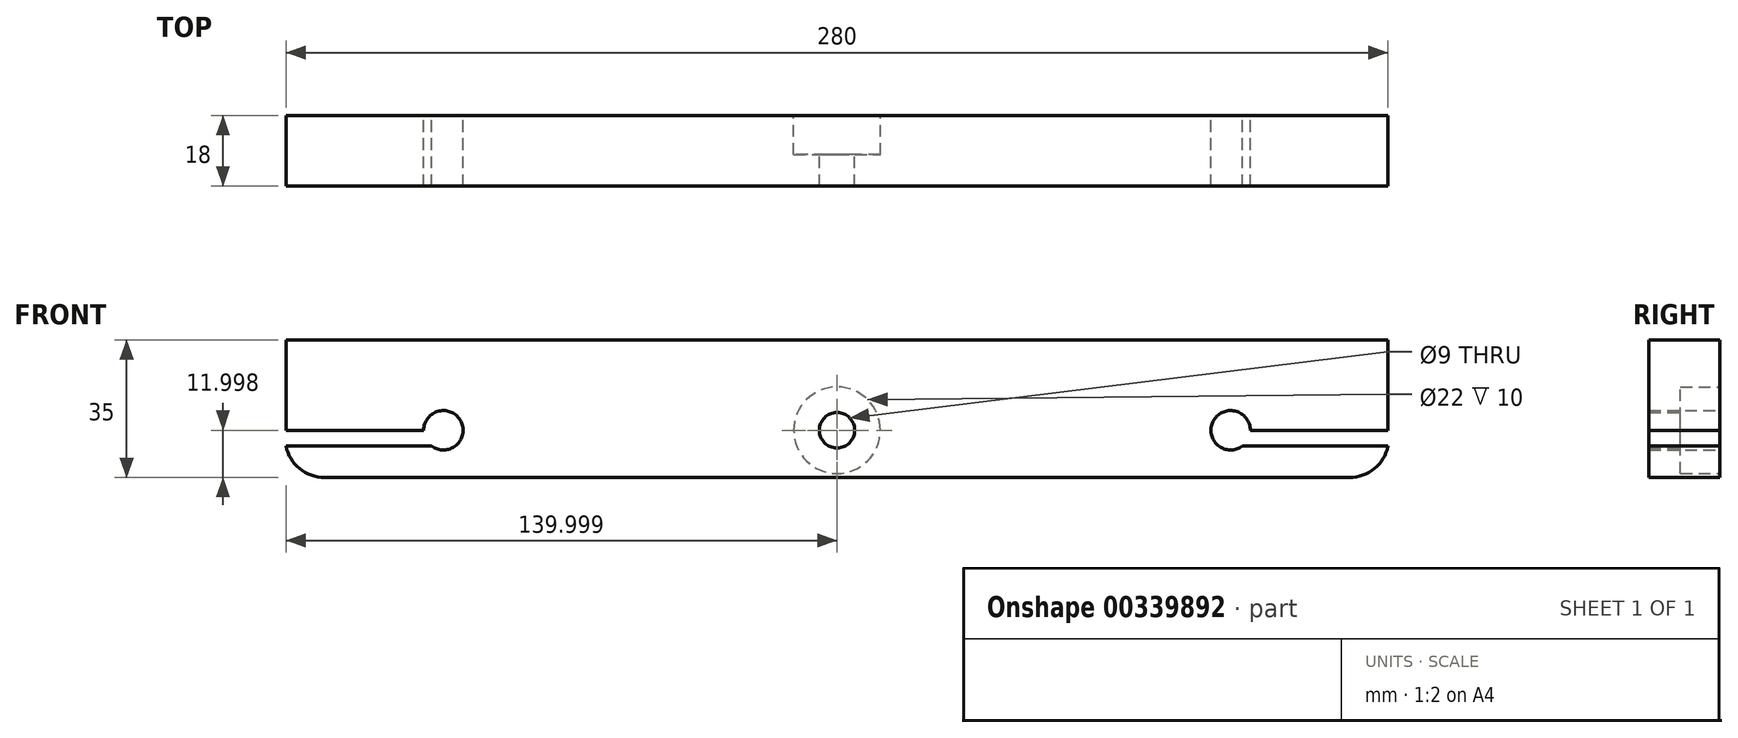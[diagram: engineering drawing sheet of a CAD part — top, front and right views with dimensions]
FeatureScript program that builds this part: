
annotation { "Feature Type Name" : "Feature", "Feature Type Description" : "" }
export const myFeature = defineFeature(function(context is Context, id is Id, definition is map)
    precondition{}
    {
        {
            var Q0;
            Q0=qCreatedBy(makeId("Front.planeOp"),FACE);
            var sketch = newSketch(context, id + "F0", { "sketchPlane" : qUnion([Q0])});
            skLineSegment(sketch, "E0.bottom", {"start": v(-327.2, -35.06) * mm, "end": v(-47.2, -35.06) * mm});
            skLineSegment(sketch, "E0.left", {"start": v(-327.2, -35.06) * mm, "end": v(-327.2, -70.06) * mm});
            skLineSegment(sketch, "E0.right", {"start": v(-47.2, -35.06) * mm, "end": v(-47.2, -70.06) * mm});
            skLineSegment(sketch, "E1", {"start": v(-327.2, -58.06) * mm, "end": v(-47.2, -58.06) * mm, "construction": true});
            skCircle(sketch, "E2", {"center": v(-187.2, -58.06) * mm, "radius": 4.5 * mm});
            skCircle(sketch, "E3", {"center": v(-287.2, -58.06) * mm, "radius": 5 * mm});
            skCircle(sketch, "E4", {"center": v(-87.2, -58.06) * mm, "radius": 5 * mm});
            skLineSegment(sketch, "E5", {"start": v(-327.2, -70.06) * mm, "end": v(-47.2, -70.06) * mm});
            skLineSegment(sketch, "E6.bottom", {"start": v(-327.2, -58.06) * mm, "end": v(-287.2, -58.06) * mm});
            skLineSegment(sketch, "E6.top", {"start": v(-327.2, -62.06) * mm, "end": v(-287.2, -62.06) * mm});
            skLineSegment(sketch, "E6.left", {"start": v(-327.2, -58.06) * mm, "end": v(-327.2, -62.06) * mm});
            skLineSegment(sketch, "E6.right", {"start": v(-287.2, -58.06) * mm, "end": v(-287.2, -62.06) * mm});
            skLineSegment(sketch, "E7.bottom", {"start": v(-47.2, -58.06) * mm, "end": v(-87.2, -58.06) * mm});
            skLineSegment(sketch, "E7.top", {"start": v(-47.2, -62.06) * mm, "end": v(-87.2, -62.06) * mm});
            skLineSegment(sketch, "E7.left", {"start": v(-47.2, -58.06) * mm, "end": v(-47.2, -62.06) * mm});
            skLineSegment(sketch, "E7.right", {"start": v(-87.2, -58.06) * mm, "end": v(-87.2, -62.06) * mm});
            skCircle(sketch, "E8", {"center": v(-187.2, -58.06) * mm, "radius": 11 * mm});
            skSolve(sketch);
        }
        {
            var Q0;
            {var subQ6=sQuery(id+"F0.wireOp",EDGE,"99775e44-fb85-472b-b0f3-04b92af737a2.bottom");Q0=makeQuery(id+"F0.imprint","IMPRINT",FACE,{"disambiguationData":[TD([[makeQuery(id+"F0.imprint","IMPRINT",EDGE,{"derivedFrom":subQ6}),-1.0]])]});}
            var Q1;
            Q1=makeQuery(id+"F0.imprint","IMPRINT",FACE,{"disambiguationData":[TD([[makeQuery(id+"F0.imprint","IMPRINT",EDGE,{"derivedFrom":sQuery(id+"F0.wireOp",EDGE,"c4dccc37-b2cb-4d1d-85ec-d6a2668cacbb")}),-1.0]])]});
            var Q2;
            {var subQ17=sQuery(id+"F0.wireOp",EDGE,"E0.bottom");Q2=makeQuery(id+"F0.imprint","IMPRINT",FACE,{"disambiguationData":[TD([[makeQuery(id+"F0.imprint","IMPRINT",EDGE,{"derivedFrom":subQ17}),-1.0]])]});}
            var Q3;
            Q3=makeQuery(id+"F0.imprint","IMPRINT",FACE,{"disambiguationData":[TD([[makeQuery(id+"F0.imprint","IMPRINT",EDGE,{"derivedFrom":sQuery(id+"F0.wireOp",EDGE,"E2")}),-1.0]])]});
            extrude(context, id + "F1", {"entities" : qUnion([Q0, Q1, Q2, Q3]), "offsetDistance" : 25 * mm, "depth" : 18 * mm});
        }
        {
            var Q0;
            Q0=makeQuery(id+"F0.imprint","IMPRINT",FACE,{"disambiguationData":[TD([[makeQuery(id+"F0.imprint","IMPRINT",EDGE,{"derivedFrom":sQuery(id+"F0.wireOp",EDGE,"E2")}),-1.0]])]});
            extrude(context, id + "F2", {"entities" : qUnion([Q0]), "operationType" : NewBodyOperationType.REMOVE, "offsetDistance" : 25 * mm, "depth" : 10 * mm});
        }
        {
            var Q0;
            Q0=makeQuery(id+"F1.opExtrude","SWEPT_EDGE",EDGE,{"disambiguationData":[OSD([sQuery(id+"F0.wireOp",EDGE,"E0.left"),sQuery(id+"F0.wireOp",EDGE,"E5")])]});
            var Q1;
            Q1=makeQuery(id+"F1.opExtrude","SWEPT_EDGE",EDGE,{"disambiguationData":[OSD([sQuery(id+"F0.wireOp",EDGE,"E0.right"),sQuery(id+"F0.wireOp",EDGE,"E5")])]});
            fillet(context, id + "F3", {"entities" : qUnion([Q0, Q1]), "radius" : 10 * mm, "tangentPropagation" : true, "allowEdgeOverflow" : false});
        }
    });
